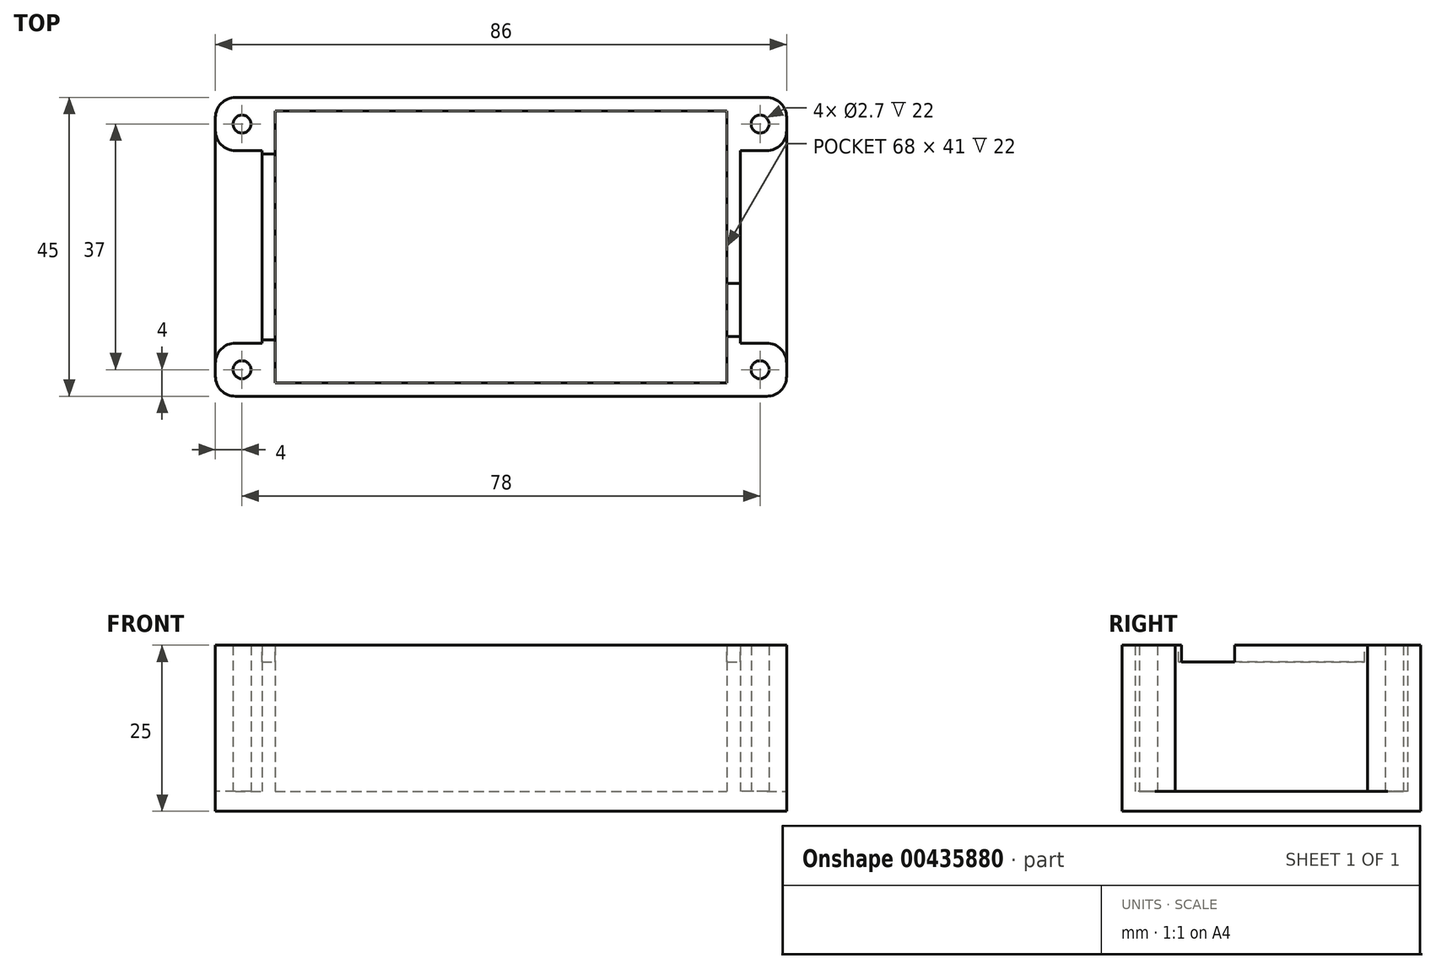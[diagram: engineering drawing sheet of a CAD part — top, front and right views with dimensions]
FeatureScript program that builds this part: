
annotation { "Feature Type Name" : "Feature", "Feature Type Description" : "" }
export const myFeature = defineFeature(function(context is Context, id is Id, definition is map)
    precondition{}
    {
        {
            var Q0;
            Q0=qCreatedBy(makeId("Top.planeOp"),FACE);
            var sketch = newSketch(context, id + "F0", { "sketchPlane" : qUnion([Q0])});
            skLineSegment(sketch, "E0.bottom", {"start": v(-43, 22.5) * mm, "end": v(43, 22.5) * mm});
            skLineSegment(sketch, "E0.top", {"start": v(-43, -22.5) * mm, "end": v(43, -22.5) * mm});
            skLineSegment(sketch, "E0.left", {"start": v(-43, 22.5) * mm, "end": v(-43, -22.5) * mm});
            skLineSegment(sketch, "E0.right", {"start": v(43, 22.5) * mm, "end": v(43, -22.5) * mm});
            skSolve(sketch);
        }
        {
            var Q0;
            Q0=qSketchRegion(id+"F0",true);
            var Q1;
            Q1 = qSketchRegion(id + "F2", true);
            extrude(context, id + "F1", {"entities" : qUnion([Q0, Q1]), "depth" : 3 * mm});
        }
        {
            var Q0;
            Q0=makeQuery(id+"F1.opExtrude","CAP_FACE",FACE,{"disambiguationData":[OSD([sQuery(id+"F0.wireOp",EDGE,"E0.bottom"),sQuery(id+"F0.wireOp",EDGE,"E0.top"),sQuery(id+"F0.wireOp",EDGE,"E0.left"),sQuery(id+"F0.wireOp",EDGE,"E0.right")])],"isStart":false});
            var sketch = newSketch(context, id + "F2", { "sketchPlane" : qUnion([Q0])});
            skLineSegment(sketch, "E1.bottom", {"start": v(-36, 22.5) * mm, "end": v(36, 22.5) * mm, "construction": true});
            skLineSegment(sketch, "E1.top", {"start": v(-36, -22.5) * mm, "end": v(36, -22.5) * mm, "construction": true});
            skLineSegment(sketch, "E1.left", {"start": v(-36, 22.5) * mm, "end": v(-36, -22.5) * mm, "construction": true});
            skLineSegment(sketch, "E1.right", {"start": v(36, 22.5) * mm, "end": v(36, -22.5) * mm, "construction": true});
            skLineSegment(sketch, "E2.0", {"start": v(-34, 20.5) * mm, "end": v(34, 20.5) * mm});
            skLineSegment(sketch, "E2.1", {"start": v(-34, 20.5) * mm, "end": v(-34, -20.5) * mm});
            skLineSegment(sketch, "E2.2", {"start": v(-34, -20.5) * mm, "end": v(34, -20.5) * mm});
            skLineSegment(sketch, "E2.3", {"start": v(34, 20.5) * mm, "end": v(34, -20.5) * mm});
            skLineSegment(sketch, "E3", {"start": v(-43, 22.5) * mm, "end": v(43, 22.5) * mm});
            skLineSegment(sketch, "E4", {"start": v(43, 22.5) * mm, "end": v(43, 14.5) * mm});
            skLineSegment(sketch, "E5", {"start": v(43, 14.5) * mm, "end": v(36, 14.5) * mm});
            skLineSegment(sketch, "E6", {"start": v(36, 14.5) * mm, "end": v(36, -14.5) * mm});
            skLineSegment(sketch, "E7", {"start": v(36, -14.5) * mm, "end": v(43, -14.5) * mm});
            skLineSegment(sketch, "E8", {"start": v(43, -14.5) * mm, "end": v(43, -22.5) * mm});
            skLineSegment(sketch, "E9", {"start": v(43, -22.5) * mm, "end": v(-43, -22.5) * mm});
            skLineSegment(sketch, "E10", {"start": v(-43, -22.5) * mm, "end": v(-43, -14.5) * mm});
            skLineSegment(sketch, "E11", {"start": v(-43, -14.5) * mm, "end": v(-36, -14.5) * mm});
            skLineSegment(sketch, "E12", {"start": v(-36, -14.5) * mm, "end": v(-36, 14.5) * mm});
            skLineSegment(sketch, "E13", {"start": v(-36, 14.5) * mm, "end": v(-43, 14.5) * mm});
            skLineSegment(sketch, "E14", {"start": v(-43, 14.5) * mm, "end": v(-43, 22.5) * mm});
            skLineSegment(sketch, "E15", {"start": v(-39, 29.97) * mm, "end": v(-39, -31.03) * mm, "construction": true});
            skCircle(sketch, "E16", {"center": v(-39, 18.5) * mm, "radius": 1.35 * mm});
            skCircle(sketch, "E17", {"center": v(-39, -18.5) * mm, "radius": 1.35 * mm});
            skCircle(sketch, "E18.MirrorC", {"center": v(39, -18.5) * mm, "radius": 1.35 * mm});
            skCircle(sketch, "E19.MirrorC", {"center": v(39, 18.5) * mm, "radius": 1.35 * mm});
            skSolve(sketch);
        }
        {
            var Q0;
            Q0=qSketchRegion(id+"F2",true);
            extrude(context, id + "F3", {"entities" : qUnion([Q0]), "operationType" : NewBodyOperationType.ADD, "depth" : 22 * mm});
        }
        {
            var Q0;
            Q0=makeQuery(id+"F3.boolean.opBoolean","MERGE",EDGE,{"derivedFrom":[makeQuery(id+"F1.opExtrude","SWEPT_EDGE",EDGE,{"disambiguationData":[OSD([sQuery(id+"F0.wireOp",EDGE,"E0.top"),sQuery(id+"F0.wireOp",EDGE,"E0.left")])]}),makeQuery(id+"F3.opExtrude","SWEPT_EDGE",EDGE,{"disambiguationData":[OSD([sQuery(id+"F2.wireOp",EDGE,"E9"),sQuery(id+"F2.wireOp",EDGE,"E10")])]})]});
            var Q1;
            Q1=makeQuery(id+"F3.opExtrude","SWEPT_EDGE",EDGE,{"disambiguationData":[OSD([sQuery(id+"F0.wireOp",EDGE,"E0.left"),sQuery(id+"F2.wireOp",EDGE,"E13"),sQuery(id+"F2.wireOp",EDGE,"E14")])]});
            var Q2;
            Q2=makeQuery(id+"F3.boolean.opBoolean","MERGE",EDGE,{"derivedFrom":[makeQuery(id+"F1.opExtrude","SWEPT_EDGE",EDGE,{"disambiguationData":[OSD([sQuery(id+"F0.wireOp",EDGE,"E0.bottom"),sQuery(id+"F0.wireOp",EDGE,"E0.left")])]}),makeQuery(id+"F3.opExtrude","SWEPT_EDGE",EDGE,{"disambiguationData":[OSD([sQuery(id+"F2.wireOp",EDGE,"E3"),sQuery(id+"F2.wireOp",EDGE,"E14")])]})]});
            var Q3;
            Q3=makeQuery(id+"F3.opExtrude","SWEPT_EDGE",EDGE,{"disambiguationData":[OSD([sQuery(id+"F0.wireOp",EDGE,"E0.left"),sQuery(id+"F2.wireOp",EDGE,"E10"),sQuery(id+"F2.wireOp",EDGE,"E11")])]});
            var Q4;
            Q4=makeQuery(id+"F3.boolean.opBoolean","MERGE",EDGE,{"derivedFrom":[makeQuery(id+"F1.opExtrude","SWEPT_EDGE",EDGE,{"disambiguationData":[OSD([sQuery(id+"F0.wireOp",EDGE,"E0.top"),sQuery(id+"F0.wireOp",EDGE,"E0.right")])]}),makeQuery(id+"F3.opExtrude","SWEPT_EDGE",EDGE,{"disambiguationData":[OSD([sQuery(id+"F2.wireOp",EDGE,"E8"),sQuery(id+"F2.wireOp",EDGE,"E9")])]})]});
            var Q5;
            Q5=makeQuery(id+"F3.opExtrude","SWEPT_EDGE",EDGE,{"disambiguationData":[OSD([sQuery(id+"F0.wireOp",EDGE,"E0.right"),sQuery(id+"F2.wireOp",EDGE,"E7"),sQuery(id+"F2.wireOp",EDGE,"E8")])]});
            var Q6;
            Q6=makeQuery(id+"F3.opExtrude","SWEPT_EDGE",EDGE,{"disambiguationData":[OSD([sQuery(id+"F0.wireOp",EDGE,"E0.right"),sQuery(id+"F2.wireOp",EDGE,"E4"),sQuery(id+"F2.wireOp",EDGE,"E5")])]});
            var Q7;
            Q7=makeQuery(id+"F3.boolean.opBoolean","MERGE",EDGE,{"derivedFrom":[makeQuery(id+"F1.opExtrude","SWEPT_EDGE",EDGE,{"disambiguationData":[OSD([sQuery(id+"F0.wireOp",EDGE,"E0.bottom"),sQuery(id+"F0.wireOp",EDGE,"E0.right")])]}),makeQuery(id+"F3.opExtrude","SWEPT_EDGE",EDGE,{"disambiguationData":[OSD([sQuery(id+"F2.wireOp",EDGE,"E3"),sQuery(id+"F2.wireOp",EDGE,"E4")])]})]});
            fillet(context, id + "F4", {"entities" : qUnion([Q0, Q1, Q2, Q3, Q4, Q5, Q6, Q7]), "radius" : 3 * mm, "tangentPropagation" : true, "allowEdgeOverflow" : false});
        }
        {
            var Q0;
            Q0=makeQuery(id+"F3.opExtrude","CAP_FACE",FACE,{"disambiguationData":[OSD([sQuery(id+"F2.wireOp",EDGE,"E2.0"),sQuery(id+"F2.wireOp",EDGE,"E2.1"),sQuery(id+"F2.wireOp",EDGE,"E2.2"),sQuery(id+"F2.wireOp",EDGE,"E2.3"),sQuery(id+"F2.wireOp",EDGE,"E3"),sQuery(id+"F2.wireOp",EDGE,"E4"),sQuery(id+"F2.wireOp",EDGE,"E5"),sQuery(id+"F2.wireOp",EDGE,"E6"),sQuery(id+"F2.wireOp",EDGE,"E7"),sQuery(id+"F2.wireOp",EDGE,"E8"),sQuery(id+"F2.wireOp",EDGE,"E9"),sQuery(id+"F2.wireOp",EDGE,"E10"),sQuery(id+"F2.wireOp",EDGE,"E11"),sQuery(id+"F2.wireOp",EDGE,"E12"),sQuery(id+"F2.wireOp",EDGE,"E13"),sQuery(id+"F2.wireOp",EDGE,"E14"),sQuery(id+"F2.wireOp",EDGE,"E16"),sQuery(id+"F2.wireOp",EDGE,"E17"),sQuery(id+"F2.wireOp",EDGE,"E18.MirrorC"),sQuery(id+"F2.wireOp",EDGE,"E19.MirrorC")])],"isStart":false});
            var sketch = newSketch(context, id + "F5", { "sketchPlane" : qUnion([Q0])});
            skLineSegment(sketch, "E20.bottom", {"start": v(-36, 14) * mm, "end": v(-34, 14) * mm});
            skLineSegment(sketch, "E20.top", {"start": v(-36, -14) * mm, "end": v(-34, -14) * mm});
            skLineSegment(sketch, "E20.left", {"start": v(-36, 14) * mm, "end": v(-36, -14) * mm});
            skLineSegment(sketch, "E20.right", {"start": v(-34, 14) * mm, "end": v(-34, -14) * mm});
            skLineSegment(sketch, "E21.bottom", {"start": v(34, -5.5) * mm, "end": v(36, -5.5) * mm});
            skLineSegment(sketch, "E21.top", {"start": v(34, -13.5) * mm, "end": v(36, -13.5) * mm});
            skLineSegment(sketch, "E21.left", {"start": v(34, -5.5) * mm, "end": v(34, -13.5) * mm});
            skLineSegment(sketch, "E21.right", {"start": v(36, -5.5) * mm, "end": v(36, -13.5) * mm});
            skLineSegment(sketch, "E22", {"start": v(15.76, -9.5) * mm, "end": v(48.31, -9.5) * mm, "construction": true});
            skSolve(sketch);
        }
        {
            var Q0;
            Q0=qSketchRegion(id+"F5",true);
            extrude(context, id + "F6", {"entities" : qUnion([Q0]), "operationType" : NewBodyOperationType.REMOVE, "oppositeDirection" : true, "depth" : 2.5 * mm});
        }
    });
